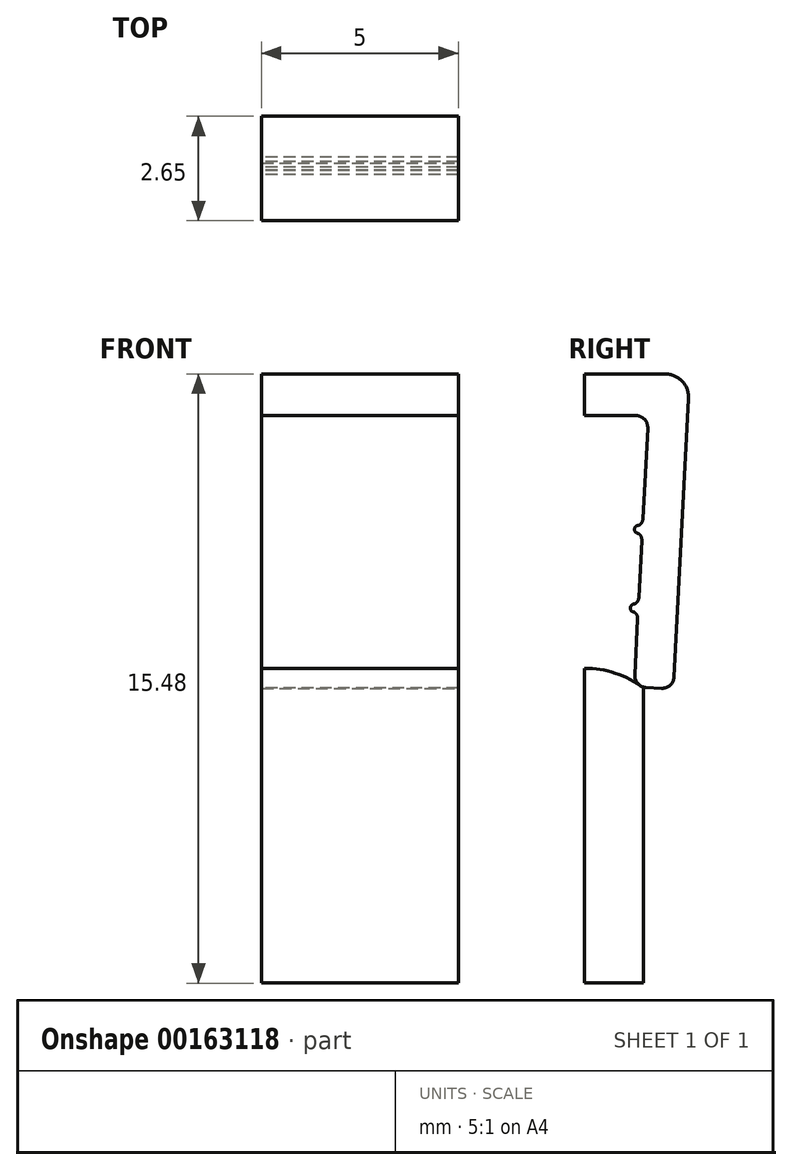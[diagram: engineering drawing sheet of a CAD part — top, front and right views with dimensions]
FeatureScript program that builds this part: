
annotation { "Feature Type Name" : "Feature", "Feature Type Description" : "" }
export const myFeature = defineFeature(function(context is Context, id is Id, definition is map)
    precondition{}
    {
        {
            var Q0;
            Q0=qCreatedBy(makeId("Right.planeOp"),FACE);
            var sketch = newSketch(context, id + "F8", { "sketchPlane" : qUnion([Q0])});
            skLineSegment(sketch, "E0", {"start": v(0, 0) * mm, "end": v(0, -6.94) * mm, "construction": true});
            skLineSegment(sketch, "E1", {"start": v(0, 0) * mm, "end": v(2.05, 0) * mm});
            skLineSegment(sketch, "E2", {"start": v(2.68, 0) * mm, "end": v(2.68, 0) * mm});
            skLineSegment(sketch, "E3", {"start": v(2.26, -8) * mm, "end": v(2.65, -0.63) * mm});
            skLineSegment(sketch, "E4", {"start": v(0, 0) * mm, "end": v(0, -1.06) * mm});
            skLineSegment(sketch, "E5", {"start": v(0, -1.06) * mm, "end": v(0, -1.06) * mm});
            skLineSegment(sketch, "E6", {"start": v(1.39, -5.65) * mm, "end": v(1.39, -5.65) * mm});
            skLineSegment(sketch, "E7", {"start": v(1.27, -7.95) * mm, "end": v(1.36, -6.14) * mm});
            skLineSegment(sketch, "E8", {"start": v(1.63, -1.06) * mm, "end": v(1.63, -1.06) * mm});
            skLineSegment(sketch, "E9", {"start": v(0, -1.06) * mm, "end": v(1.63, -1.06) * mm});
            skLineSegment(sketch, "E10", {"start": v(2.26, -8) * mm, "end": v(1.27, -7.95) * mm});
            skLineSegment(sketch, "E11", {"start": v(2.53, -4.12) * mm, "end": v(2.53, -4.12) * mm});
            skLineSegment(sketch, "E12", {"start": v(0.89, -5.93) * mm, "end": v(3.18, -6.05) * mm, "construction": true});
            skLineSegment(sketch, "E13", {"start": v(1.27, -6.05) * mm, "end": v(1.36, -6.14) * mm});
            skLineSegment(sketch, "E14.MirrorCS", {"start": v(1.29, -5.85) * mm, "end": v(1.38, -5.76) * mm});
            skLineSegment(sketch, "E15.trimOffspring", {"start": v(1.38, -5.76) * mm, "end": v(1.46, -4.14) * mm});
            skPoint(sketch, "E16.MirrorCS.end.orphan", {"position": v(1.2, -5.94) * mm});
            skPoint(sketch, "E16.MirrorCS.start.orphan", {"position": v(1.29, -5.85) * mm});
            skLineSegment(sketch, "E17", {"start": v(1.29, -5.85) * mm, "end": v(1.18, -5.84) * mm});
            skLineSegment(sketch, "E18.MirrorCS", {"start": v(1.27, -6.05) * mm, "end": v(1.16, -6.04) * mm});
            skLineSegment(sketch, "E19", {"start": v(1.18, -5.84) * mm, "end": v(1.16, -6.04) * mm});
            skPoint(sketch, "E20.visualSharp", {"position": v(2.68, 0) * mm});
            skArc(sketch, "E20.filletArc", {"start": v(2.65, -0.63) * mm, "mid": v(2.49, -0.19) * mm, "end": v(2.05, 0) * mm});
            skLineSegment(sketch, "E21", {"start": v(1.15, -3.94) * mm, "end": v(2.96, -4.03) * mm, "construction": true});
            skLineSegment(sketch, "E22", {"start": v(1.48, -3.76) * mm, "end": v(1.39, -3.85) * mm});
            skLineSegment(sketch, "E23", {"start": v(1.39, -3.85) * mm, "end": v(1.39, -3.85) * mm});
            skLineSegment(sketch, "E24", {"start": v(1.28, -3.84) * mm, "end": v(1.39, -3.85) * mm});
            skLineSegment(sketch, "E25.MirrorCS", {"start": v(1.46, -4.14) * mm, "end": v(1.38, -4.05) * mm});
            skLineSegment(sketch, "E26.MirrorCS", {"start": v(1.27, -4.04) * mm, "end": v(1.38, -4.05) * mm});
            skLineSegment(sketch, "E27", {"start": v(1.27, -4.04) * mm, "end": v(1.28, -3.84) * mm});
            skLineSegment(sketch, "E28.trimOffspring", {"start": v(1.48, -3.76) * mm, "end": v(1.63, -1.06) * mm});
            skSolve(sketch);
        }
        {
            var Q0;
            Q0 = qSketchRegion(id + "F8", true);
            extrude(context, id + "F0", {"entities" : qUnion([Q0]), "depth" : 5 * mm});
        }
        {
            var Q0;
            Q0=makeQuery(id+"F0.opExtrude","SWEPT_EDGE",EDGE,{"disambiguationData":[OSD([sQuery(id+"F8.wireOp",EDGE,"E7"),sQuery(id+"F8.wireOp",EDGE,"E10")])]});
            var Q1;
            Q1=makeQuery(id+"F0.opExtrude","SWEPT_EDGE",EDGE,{"disambiguationData":[OSD([sQuery(id+"F8.wireOp",EDGE,"E3"),sQuery(id+"F8.wireOp",EDGE,"E10")])]});
            fillet(context, id + "F1", {"entities" : qUnion([Q0, Q1]), "radius" : 0.3 * mm, "tangentPropagation" : true, "allowEdgeOverflow" : false});
        }
        {
            var Q0;
            Q0=makeQuery(id+"F0.opExtrude","SWEPT_EDGE",EDGE,{"disambiguationData":[OSD([sQuery(id+"F8.wireOp",EDGE,"E13"),sQuery(id+"F8.wireOp",EDGE,"E18.MirrorCS")])]});
            fillet(context, id + "F2", {"entities" : qUnion([Q0]), "radius" : 0.1 * mm, "tangentPropagation" : true, "allowEdgeOverflow" : false});
        }
        {
            var Q0;
            Q0=makeQuery(id+"F0.opExtrude","SWEPT_EDGE",EDGE,{"disambiguationData":[OSD([sQuery(id+"F8.wireOp",EDGE,"E7"),sQuery(id+"F8.wireOp",EDGE,"E13")])]});
            fillet(context, id + "F9", {"entities" : qUnion([Q0]), "radius" : 0.2 * mm, "tangentPropagation" : true, "allowEdgeOverflow" : false});
        }
        {
            var Q0;
            Q0=makeQuery(id+"F0.opExtrude","SWEPT_EDGE",EDGE,{"disambiguationData":[OSD([sQuery(id+"F8.wireOp",EDGE,"E14.MirrorCS"),sQuery(id+"F8.wireOp",EDGE,"E17")])]});
            fillet(context, id + "F10", {"entities" : qUnion([Q0]), "radius" : 0.1 * mm, "tangentPropagation" : true, "allowEdgeOverflow" : false});
        }
        {
            var Q0;
            Q0=makeQuery(id+"F0.opExtrude","SWEPT_EDGE",EDGE,{"disambiguationData":[OSD([sQuery(id+"F8.wireOp",EDGE,"E17"),sQuery(id+"F8.wireOp",EDGE,"E19")])]});
            var Q1;
            Q1=makeQuery(id+"F0.opExtrude","SWEPT_EDGE",EDGE,{"disambiguationData":[OSD([sQuery(id+"F8.wireOp",EDGE,"E18.MirrorCS"),sQuery(id+"F8.wireOp",EDGE,"E19")])]});
            fillet(context, id + "F3", {"entities" : qUnion([Q0, Q1]), "radius" : 0.1 * mm, "tangentPropagation" : true, "allowEdgeOverflow" : false});
        }
        {
            var Q0;
            Q0=makeQuery(id+"F0.opExtrude","SWEPT_EDGE",EDGE,{"disambiguationData":[OSD([sQuery(id+"F8.wireOp",EDGE,"E14.MirrorCS"),sQuery(id+"F8.wireOp",EDGE,"E15.trimOffspring")])]});
            fillet(context, id + "F4", {"entities" : qUnion([Q0]), "radius" : 0.2 * mm, "tangentPropagation" : true, "allowEdgeOverflow" : false});
        }
        {
            var Q0;
            Q0=makeQuery(id+"F0.opExtrude","SWEPT_EDGE",EDGE,{"disambiguationData":[OSD([sQuery(id+"F8.wireOp",EDGE,"E15.trimOffspring"),sQuery(id+"F8.wireOp",EDGE,"E25.MirrorCS")])]});
            var Q1;
            Q1=makeQuery(id+"F0.opExtrude","SWEPT_EDGE",EDGE,{"disambiguationData":[OSD([sQuery(id+"F8.wireOp",EDGE,"E22"),sQuery(id+"F8.wireOp",EDGE,"E28.trimOffspring")])]});
            fillet(context, id + "F5", {"entities" : qUnion([Q0, Q1]), "radius" : 0.2 * mm, "tangentPropagation" : true, "allowEdgeOverflow" : false});
        }
        {
            var Q0;
            Q0=makeQuery(id+"F0.opExtrude","SWEPT_EDGE",EDGE,{"disambiguationData":[OSD([sQuery(id+"F8.wireOp",EDGE,"E25.MirrorCS"),sQuery(id+"F8.wireOp",EDGE,"E26.MirrorCS")])]});
            var Q1;
            Q1=makeQuery(id+"F0.opExtrude","SWEPT_EDGE",EDGE,{"disambiguationData":[OSD([sQuery(id+"F8.wireOp",EDGE,"E22"),sQuery(id+"F8.wireOp",EDGE,"E24")])]});
            fillet(context, id + "F6", {"entities" : qUnion([Q0, Q1]), "radius" : 0.1 * mm, "tangentPropagation" : true, "allowEdgeOverflow" : false});
        }
        {
            var Q0;
            Q0=makeQuery(id+"F0.opExtrude","SWEPT_EDGE",EDGE,{"disambiguationData":[OSD([sQuery(id+"F8.wireOp",EDGE,"E26.MirrorCS"),sQuery(id+"F8.wireOp",EDGE,"E27")])]});
            var Q1;
            Q1=makeQuery(id+"F0.opExtrude","SWEPT_EDGE",EDGE,{"disambiguationData":[OSD([sQuery(id+"F8.wireOp",EDGE,"E24"),sQuery(id+"F8.wireOp",EDGE,"E27")])]});
            fillet(context, id + "F11", {"entities" : qUnion([Q0, Q1]), "radius" : 0.1 * mm, "tangentPropagation" : true, "allowEdgeOverflow" : false});
        }
        {
            var Q0;
            Q0=makeQuery(id+"F0.opExtrude","SWEPT_EDGE",EDGE,{"disambiguationData":[OSD([sQuery(id+"F8.wireOp",EDGE,"E9"),sQuery(id+"F8.wireOp",EDGE,"E28.trimOffspring")])]});
            fillet(context, id + "F7", {"entities" : qUnion([Q0]), "radius" : 0.3 * mm, "tangentPropagation" : true, "allowEdgeOverflow" : false});
        }
        {
            var Q0;
            Q0=qCreatedBy(makeId("Right.planeOp"),FACE);
            var sketch = newSketch(context, id + "F12", { "sketchPlane" : qUnion([Q0])});
            skLineSegment(sketch, "E29", {"start": v(0, 0) * mm, "end": v(0, -7.48) * mm, "construction": true});
            skLineSegment(sketch, "E30.right", {"start": v(1.5, -7.98) * mm, "end": v(1.5, -15.48) * mm});
            skArc(sketch, "E31", {"start": v(1.5, -7.98) * mm, "mid": v(0.8, -7.6) * mm, "end": v(0, -7.48) * mm});
            skLineSegment(sketch, "E32", {"start": v(0, -15.48) * mm, "end": v(1.5, -15.48) * mm});
            skLineSegment(sketch, "E33.trimOffspring", {"start": v(0, -7.48) * mm, "end": v(0, -15.48) * mm});
            skSolve(sketch);
        }
        {
            var Q0;
            Q0=makeQuery(id+"F12.imprint","IMPRINT",FACE,{"disambiguationData":[TD([[makeQuery(id+"F12.imprint","IMPRINT",EDGE,{"derivedFrom":sQuery(id+"F12.wireOp",EDGE,"E30.right")}),-1.0]])]});
            extrude(context, id + "F13", {"entities" : qUnion([Q0]), "depth" : 5 * mm});
        }
    });
